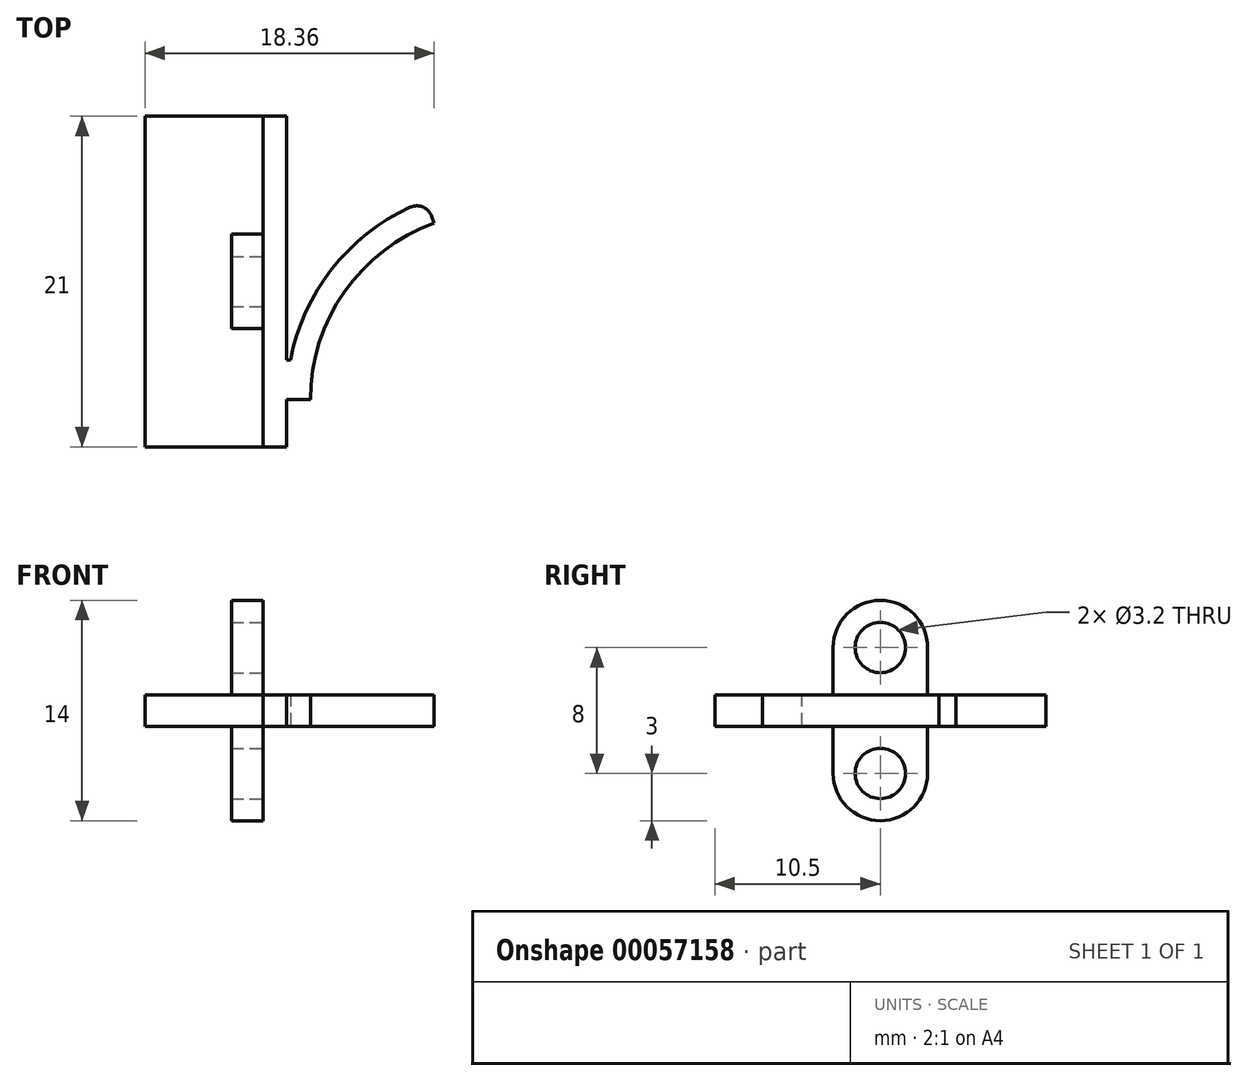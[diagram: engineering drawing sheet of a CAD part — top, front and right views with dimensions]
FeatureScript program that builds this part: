
annotation { "Feature Type Name" : "Feature", "Feature Type Description" : "" }
export const myFeature = defineFeature(function(context is Context, id is Id, definition is map)
    precondition{}
    {
        {
            var Q0;
            Q0=qCreatedBy(makeId("Top.planeOp"),FACE);
            var sketch = newSketch(context, id + "F0", { "sketchPlane" : qUnion([Q0])});
            skCircle(sketch, "E0", {"center": v(0, 0) * mm, "radius": 11.94 * mm, "construction": true});
            skLineSegment(sketch, "E1", {"start": v(-11.94, 0) * mm, "end": v(-13.44, 0) * mm});
            skLineSegment(sketch, "E2", {"start": v(-13.44, 0) * mm, "end": v(-13.44, -3) * mm});
            skLineSegment(sketch, "E3", {"start": v(-13.44, -3) * mm, "end": v(-14.94, -3) * mm});
            skLineSegment(sketch, "E4", {"start": v(-14.94, -3) * mm, "end": v(-14.94, 18) * mm});
            skLineSegment(sketch, "E5", {"start": v(-14.94, 18) * mm, "end": v(-13.44, 18) * mm});
            skLineSegment(sketch, "E6", {"start": v(-13.44, 18) * mm, "end": v(-13.44, 0) * mm});
            skLineSegment(sketch, "E7", {"start": v(0, 0) * mm, "end": v(-4.08, 11.22) * mm, "construction": true});
            skCircle(sketch, "E8", {"center": v(0, 0) * mm, "radius": 8.64 * mm, "construction": true});
            skLineSegment(sketch, "E9", {"start": v(-4.08, 11.22) * mm, "end": v(-4.24, 11.65) * mm});
            skArc(sketch, "E10", {"start": v(-11.94, 0) * mm, "mid": v(-9.78, 6.85) * mm, "end": v(-4.08, 11.22) * mm});
            skArc(sketch, "E11", {"start": v(-13.44, 0) * mm, "mid": v(-11.3, 7.26) * mm, "end": v(-5.6, 12.22) * mm});
            skLineSegment(sketch, "E12", {"start": v(-13.44, 2.5) * mm, "end": v(-13.2, 2.5) * mm});
            skPoint(sketch, "E13.visualSharp", {"position": v(-4.6, 12.63) * mm});
            skArc(sketch, "E13.filletArc", {"start": v(-4.24, 11.65) * mm, "mid": v(-4.8, 12.23) * mm, "end": v(-5.6, 12.22) * mm});
            skSolve(sketch);
        }
        {
            var Q0;
            Q0 = qSketchRegion(id + "F0", true);
            extrude(context, id + "F1", {"entities" : qUnion([Q0]), "endBound" : BoundingType.SYMMETRIC, "depth" : 2 * mm});
        }
        {
            var Q0;
            Q0=makeQuery(id+"F1.opExtrude","SWEPT_FACE",FACE,{"disambiguationData":[OSD([sQuery(id+"F0.wireOp",EDGE,"E4")])]});
            var sketch = newSketch(context, id + "F2", { "sketchPlane" : qUnion([Q0])});
            skLineSegment(sketch, "E14.0.0", {"start": v(-18, -1) * mm, "end": v(3, -1) * mm});
            skLineSegment(sketch, "E14.0.1", {"start": v(3, -1) * mm, "end": v(3, 1) * mm});
            skLineSegment(sketch, "E14.0.2", {"start": v(3, 1) * mm, "end": v(-18, 1) * mm});
            skLineSegment(sketch, "E14.0.3", {"start": v(-18, 1) * mm, "end": v(-18, -1) * mm});
            skLineSegment(sketch, "E15", {"start": v(-7.5, 1) * mm, "end": v(-7.5, 4) * mm, "construction": true});
            skLineSegment(sketch, "E16", {"start": v(-7.5, -1) * mm, "end": v(-7.5, -4) * mm, "construction": true});
            skCircle(sketch, "E17", {"center": v(-7.5, 4) * mm, "radius": 1.6 * mm});
            skCircle(sketch, "E18", {"center": v(-7.5, -4) * mm, "radius": 1.6 * mm});
            skArc(sketch, "E19", {"start": v(-10.5, 4) * mm, "mid": v(-7.5, 7) * mm, "end": v(-4.5, 4) * mm});
            skArc(sketch, "E20", {"start": v(-10.5, -4) * mm, "mid": v(-7.5, -7) * mm, "end": v(-4.5, -4) * mm});
            skLineSegment(sketch, "E21", {"start": v(-10.5, 4) * mm, "end": v(-10.5, 1) * mm});
            skLineSegment(sketch, "E22", {"start": v(-10.5, -4) * mm, "end": v(-10.5, -1) * mm});
            skLineSegment(sketch, "E23", {"start": v(-4.5, -4) * mm, "end": v(-4.5, -1) * mm});
            skLineSegment(sketch, "E24", {"start": v(-4.5, 4) * mm, "end": v(-4.5, 1) * mm});
            skSolve(sketch);
        }
        {
            var Q0;
            Q0 = qSketchRegion(id + "F2", true);
            extrude(context, id + "F3", {"entities" : qUnion([Q0]), "depth" : 2 * mm});
        }
        {
            var Q0;
            Q0=makeQuery(id+"F3.opExtrude","CAP_FACE",FACE,{"disambiguationData":[OSD([sQuery(id+"F2.wireOp",EDGE,"E14.0.0"),sQuery(id+"F2.wireOp",EDGE,"E14.0.1"),sQuery(id+"F2.wireOp",EDGE,"E14.0.2"),sQuery(id+"F2.wireOp",EDGE,"E14.0.3"),sQuery(id+"F2.wireOp",EDGE,"E17"),sQuery(id+"F2.wireOp",EDGE,"E18"),sQuery(id+"F2.wireOp",EDGE,"E19"),sQuery(id+"F2.wireOp",EDGE,"E20"),sQuery(id+"F2.wireOp",EDGE,"E21"),sQuery(id+"F2.wireOp",EDGE,"E22"),sQuery(id+"F2.wireOp",EDGE,"E23"),sQuery(id+"F2.wireOp",EDGE,"E24")])],"isStart":false});
            var sketch = newSketch(context, id + "F4", { "sketchPlane" : qUnion([Q0])});
            skLineSegment(sketch, "E25.0.0", {"start": v(-18, -1) * mm, "end": v(3, -1) * mm});
            skLineSegment(sketch, "E25.0.1", {"start": v(3, -1) * mm, "end": v(3, 1) * mm});
            skLineSegment(sketch, "E25.0.2", {"start": v(3, 1) * mm, "end": v(-18, 1) * mm});
            skLineSegment(sketch, "E25.0.3", {"start": v(-18, 1) * mm, "end": v(-18, -1) * mm});
            skSolve(sketch);
        }
        {
            var Q0;
            {var subQ0=sQuery(id+"F4.wireOp",EDGE,"E25.0.1");Q0=makeQuery(id+"F4.imprint","IMPRINT",FACE,{"disambiguationData":[TD([[makeQuery(id+"F4.imprint","IMPRINT",EDGE,{"derivedFrom":subQ0}),-1.0]])]});}
            extrude(context, id + "F5", {"entities" : qUnion([Q0]), "operationType" : NewBodyOperationType.ADD, "depth" : (6 - 0.5) * mm});
        }
    });
